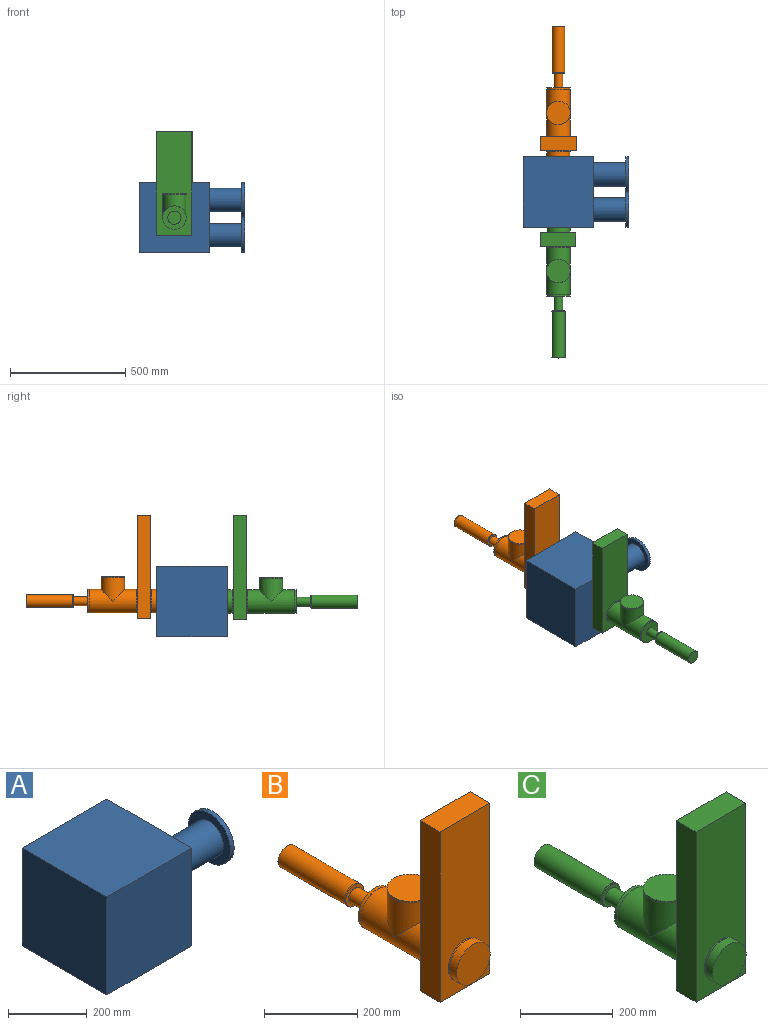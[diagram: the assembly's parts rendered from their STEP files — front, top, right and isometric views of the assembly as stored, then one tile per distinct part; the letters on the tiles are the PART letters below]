
ASSEMBLY  parts=3 mates=2
PART A: 14 faces, bbox 457.2x304.8x304.8 mm
  f0: plane 304.8x304.8mm, normal (0,-1,0), area 92903mm2, adj f1,f3,f4,f5
  f1: plane 304.8x304.8mm, normal (0,0,-1), area 92903mm2, adj f0,f2,f4,f5
  f2: plane 304.8x304.8mm, normal (0,1,0), area 92903mm2, adj f1,f3,f4,f5
  f3: plane 304.8x304.8mm, normal (0,0,1), area 92903mm2, adj f0,f2,f4,f5
  f4: plane 304.8x304.8mm, normal (1,0,0), area 76688.4mm2, adj f0,f1,f2,f3,f6,f7
  f5: plane 304.8x304.8mm, normal (-1,0,0), area 92903mm2, adj f0,f1,f2,f3
  f6: cylinder r=50.8mm len=139.7mm, axis (-1,0,0), area 44590.3mm2, adj f4,f10
  f7: cylinder r=50.8mm len=139.7mm, axis (-1,0,0), area 44590.3mm2, adj f4,f13
  f8: cylinder r=76.2mm len=152.4mm, axis (-1,0,0), area 6080.5mm2, adj f9,f10
  f9: plane 152.4x152.4mm, normal (1,0,0), area 18241.5mm2, adj f8
  f10: plane 152.4x152.4mm, normal (-1,0,0), area 10134.1mm2, adj f6,f8
  f11: cylinder r=76.2mm len=152.4mm, axis (-1,0,0), area 6080.5mm2, adj f12,f13
  f12: plane 152.4x152.4mm, normal (1,0,0), area 18241.5mm2, adj f11
  f13: plane 152.4x152.4mm, normal (-1,0,0), area 10134.1mm2, adj f7,f11
PART B: 26 faces, bbox 151.9x566.6x448.8 mm
  f0: cylinder r=50.8mm len=202.18mm, axis (0,-1,0), area 54211.7mm2, adj f12,f14,f15
  f1: cylinder r=50.8mm len=101.6mm, axis (0,-1,0), area 6891.2mm2, adj f2,f4
  f2: plane 101.6x101.6mm, normal (0,-1,0), area 8107.3mm2, adj f1
  f3: cylinder r=51mm len=102.01mm, axis (0,-1,0), area 1221mm2, adj f4,f10
  f4: plane 102.01x102.01mm, normal (0,-1,0), area 65mm2, adj f1,f3
  f5: plane 448.82x59.94mm, normal (1,0,0), area 26903.9mm2, adj f6,f8,f9,f10
  f6: plane 151.89x59.94mm, normal (0,0,-1), area 9105mm2, adj f5,f7,f9,f10
  f7: plane 448.82x59.94mm, normal (-1,0,0), area 26903.9mm2, adj f6,f8,f9,f10
  f8: plane 151.89x59.94mm, normal (0,0,1), area 9105mm2, adj f5,f7,f9,f10
  f9: plane 448.82x151.89mm, normal (0,1,0), area 59999.6mm2, adj f5,f6,f7,f8,f11
  f10: plane 448.82x151.89mm, normal (0,-1,0), area 59999.6mm2, adj f3,f5,f6,f7,f8
  f11: cylinder r=51mm len=102.01mm, axis (0,-1,0), area 1221mm2, adj f9,f12
  f12: plane 102.01x102.01mm, normal (0,1,0), area 65mm2, adj f0,f11
  f13: cylinder r=51mm len=102.01mm, axis (0,-1,0), area 2441.9mm2, adj f14,f19
  f14: plane 102.01x102.01mm, normal (0,-1,0), area 65mm2, adj f0,f13
  f15: cylinder r=50.8mm len=101.6mm, axis (0,0,-1), area 21944.6mm2, adj f0,f18
  f16: cylinder r=51mm len=102.01mm, axis (0,0,-1), area 1221mm2, adj f17,f18
  f17: plane 102.01x102.01mm, normal (0,0,1), area 8172.3mm2, adj f16
  f18: plane 102.01x102.01mm, normal (0,0,-1), area 65mm2, adj f15,f16
  f19: plane 102.01x102.01mm, normal (0,1,0), area 7032.2mm2, adj f13,f20
  f20: cylinder r=19.05mm len=61.4mm, axis (0,-1,0), area 7349.8mm2, adj f19,f23
  f21: cylinder r=27.43mm len=54.86mm, axis (0,-1,0), area 525.4mm2, adj f22,f23
  f22: plane 54.86x54.86mm, normal (0,1,0), area 8.9mm2, adj f21,f24
  f23: plane 54.86x54.86mm, normal (0,-1,0), area 1224mm2, adj f20,f21
  f24: cylinder r=27.38mm len=203.2mm, axis (0,-1,0), area 34957.3mm2, adj f22,f25
  f25: plane 54.76x54.76mm, normal (0,1,0), area 2355.2mm2, adj f24
PART C: 26 faces, bbox 151.9x566.6x448.8 mm
  f0: cylinder r=50.8mm len=202.18mm, axis (0,-1,0), area 54211.7mm2, adj f12,f14,f15
  f1: cylinder r=50.8mm len=101.6mm, axis (0,-1,0), area 6891.2mm2, adj f2,f4
  f2: plane 101.6x101.6mm, normal (0,-1,0), area 8107.3mm2, adj f1
  f3: cylinder r=51mm len=102.01mm, axis (0,-1,0), area 1221mm2, adj f4,f10
  f4: plane 102.01x102.01mm, normal (0,-1,0), area 65mm2, adj f1,f3
  f5: plane 448.82x59.94mm, normal (1,0,0), area 26903.9mm2, adj f6,f8,f9,f10
  f6: plane 151.89x59.94mm, normal (0,0,-1), area 9105mm2, adj f5,f7,f9,f10
  f7: plane 448.82x59.94mm, normal (-1,0,0), area 26903.9mm2, adj f6,f8,f9,f10
  f8: plane 151.89x59.94mm, normal (0,0,1), area 9105mm2, adj f5,f7,f9,f10
  f9: plane 448.82x151.89mm, normal (0,1,0), area 59999.6mm2, adj f5,f6,f7,f8,f11
  f10: plane 448.82x151.89mm, normal (0,-1,0), area 59999.6mm2, adj f3,f5,f6,f7,f8
  f11: cylinder r=51mm len=102.01mm, axis (0,-1,0), area 1221mm2, adj f9,f12
  f12: plane 102.01x102.01mm, normal (0,1,0), area 65mm2, adj f0,f11
  f13: cylinder r=51mm len=102.01mm, axis (0,-1,0), area 2441.9mm2, adj f14,f19
  f14: plane 102.01x102.01mm, normal (0,-1,0), area 65mm2, adj f0,f13
  f15: cylinder r=50.8mm len=101.6mm, axis (0,0,-1), area 21944.6mm2, adj f0,f18
  f16: cylinder r=51mm len=102.01mm, axis (0,0,-1), area 1221mm2, adj f17,f18
  f17: plane 102.01x102.01mm, normal (0,0,1), area 8172.3mm2, adj f16
  f18: plane 102.01x102.01mm, normal (0,0,-1), area 65mm2, adj f15,f16
  f19: plane 102.01x102.01mm, normal (0,1,0), area 7032.2mm2, adj f13,f20
  f20: cylinder r=19.05mm len=61.4mm, axis (0,-1,0), area 7349.8mm2, adj f19,f22
  f21: cylinder r=27.43mm len=54.86mm, axis (0,-1,0), area 525.4mm2, adj f22,f25
  f22: plane 54.86x54.86mm, normal (0,-1,0), area 1224mm2, adj f20,f21
  f23: cylinder r=28.57mm len=203.2mm, axis (0,-1,0), area 36480.9mm2, adj f24,f25
  f24: plane 57.15x57.15mm, normal (0,1,0), area 2564.9mm2, adj f23
  f25: plane 57.15x57.15mm, normal (0,-1,0), area 200.8mm2, adj f21,f23
PLACE A rot(axis=(0,0,-1),0deg) t=(-715.47,-698.84,-306.87)mm
PLACE B t=(97.63,-711.2,-434.26)mm
PLACE C rot(axis=(0,0,1),180deg) t=(114.58,-1397.68,-436.41)mm
MATE planar A.f2 <-> B.f0  axis (0,1,0) through (105.95,-394.04,-284.01)mm
MATE planar A.f0 <-> C.f0  axis (0,-1,0) through (105.95,-698.84,-284.01)mm
